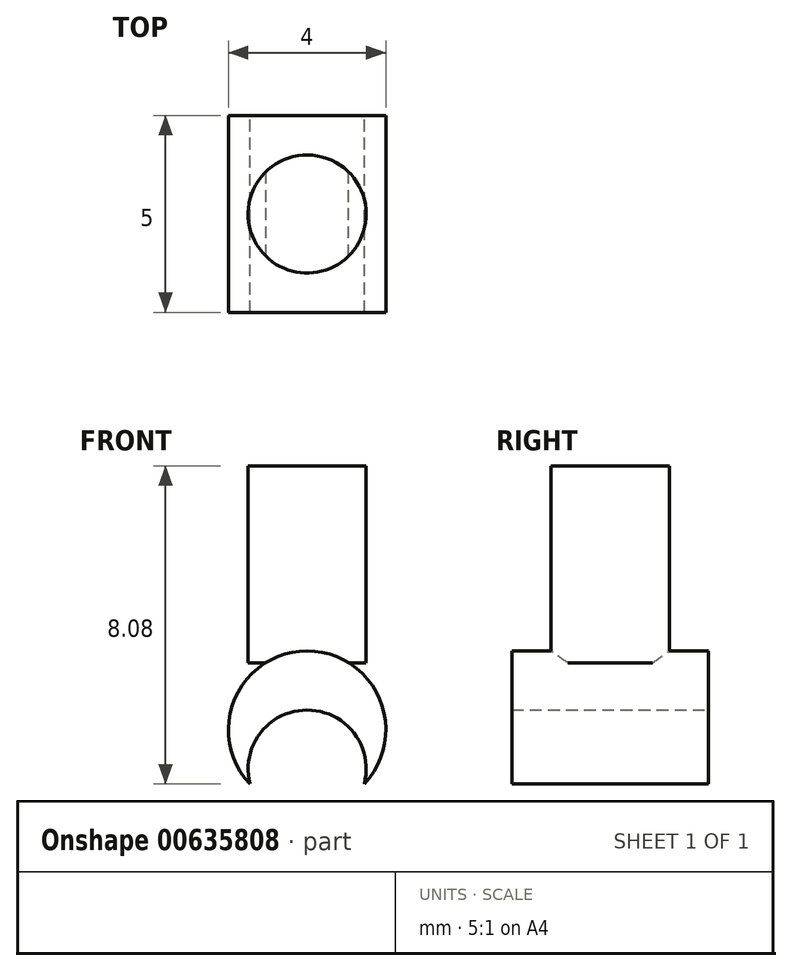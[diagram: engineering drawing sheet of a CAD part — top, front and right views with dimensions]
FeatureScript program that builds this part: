
annotation { "Feature Type Name" : "Feature", "Feature Type Description" : "" }
export const myFeature = defineFeature(function(context is Context, id is Id, definition is map)
    precondition{}
    {
        {
            var Q0;
            Q0=qCreatedBy(makeId("Front.planeOp"),FACE);
            var sketch = newSketch(context, id + "F0", { "sketchPlane" : qUnion([Q0])});
            skArc(sketch, "E0", {"start": v(1.45, -3.08) * mm, "mid": v(0, 0.3) * mm, "end": v(-1.45, -3.08) * mm});
            skArc(sketch, "E1", {"start": v(1.45, -3.08) * mm, "mid": v(0, -1.2) * mm, "end": v(-1.45, -3.08) * mm});
            skSolve(sketch);
        }
        {
            var Q0;
            Q0=makeQuery(id+"F0.imprint","IMPRINT",FACE,{"disambiguationData":[TD([[makeQuery(id+"F0.imprint","IMPRINT",EDGE,{"derivedFrom":sQuery(id+"F0.wireOp",EDGE,"E0")}),1.0]])]});
            extrude(context, id + "F1", {"entities" : qUnion([Q0]), "endBound" : BoundingType.SYMMETRIC, "depth" : 5 * mm, "offsetDistance" : 25.4 * mm});
        }
        {
            var Q0;
            Q0=qCreatedBy(makeId("Top.planeOp"),FACE);
            var sketch = newSketch(context, id + "F2", { "sketchPlane" : qUnion([Q0])});
            skCircle(sketch, "E2", {"center": v(0, 0) * mm, "radius": 1.5 * mm});
            skSolve(sketch);
        }
        {
            var Q0;
            Q0 = qSketchRegion(id + "F2", true);
            extrude(context, id + "F3", {"entities" : qUnion([Q0]), "operationType" : NewBodyOperationType.ADD, "depth" : 5 * mm, "offsetDistance" : 25.4 * mm});
        }
    });
